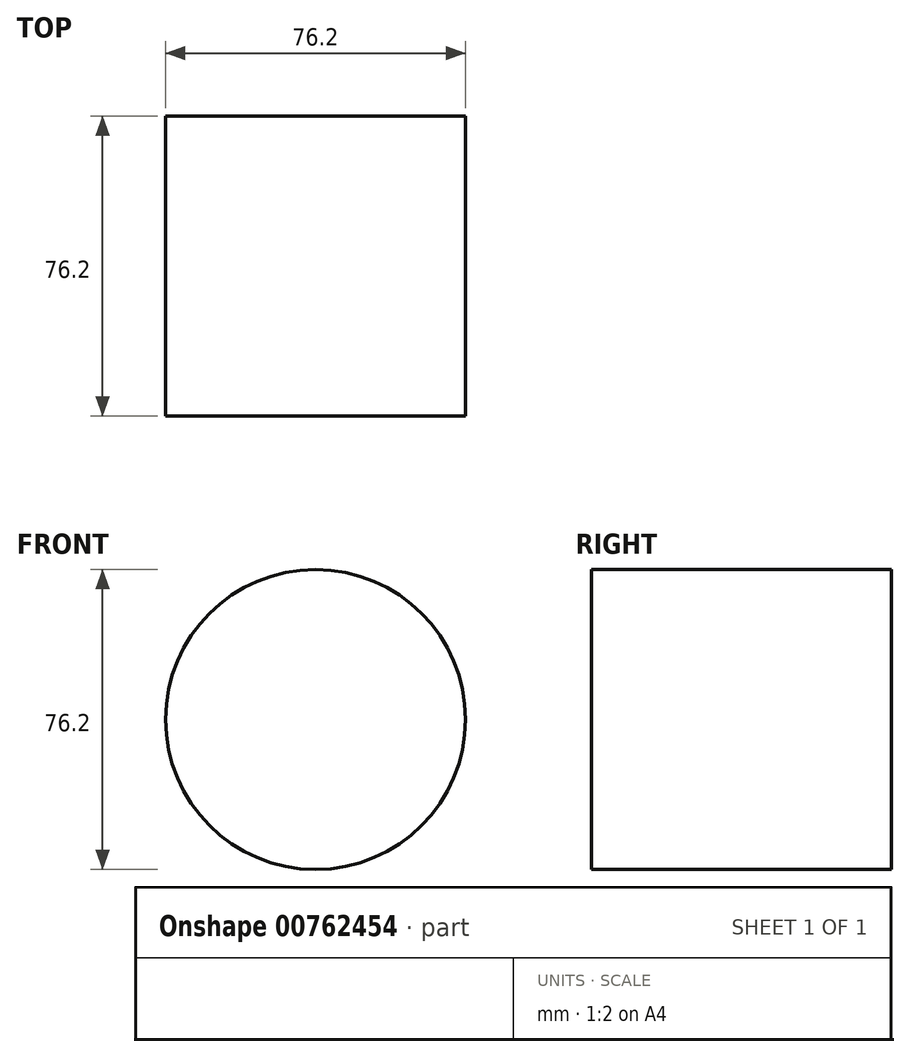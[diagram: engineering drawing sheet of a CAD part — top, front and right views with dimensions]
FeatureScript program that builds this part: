
annotation { "Feature Type Name" : "Feature", "Feature Type Description" : "" }
export const myFeature = defineFeature(function(context is Context, id is Id, definition is map)
    precondition{}
    {
        {
            var Q0;
            Q0=qCreatedBy(makeId("Front.planeOp"),FACE);
            var sketch = newSketch(context, id + "F0", { "sketchPlane" : qUnion([Q0])});
            skCircle(sketch, "E0", {"center": v(-17.96, 36.06) * mm, "radius": 38.1 * mm});
            skSolve(sketch);
        }
        {
            var Q0;
            Q0=makeQuery(id+"F0.imprint","IMPRINT",FACE,{"disambiguationData":[TD([[makeQuery(id+"F0.imprint","IMPRINT",EDGE,{"derivedFrom":sQuery(id+"F0.wireOp",EDGE,"E0")}),1.0]])]});
            extrude(context, id + "F1", {"entities" : qUnion([Q0]), "depth" : 76.2 * mm, "offsetDistance" : 25.4 * mm});
        }
    });
